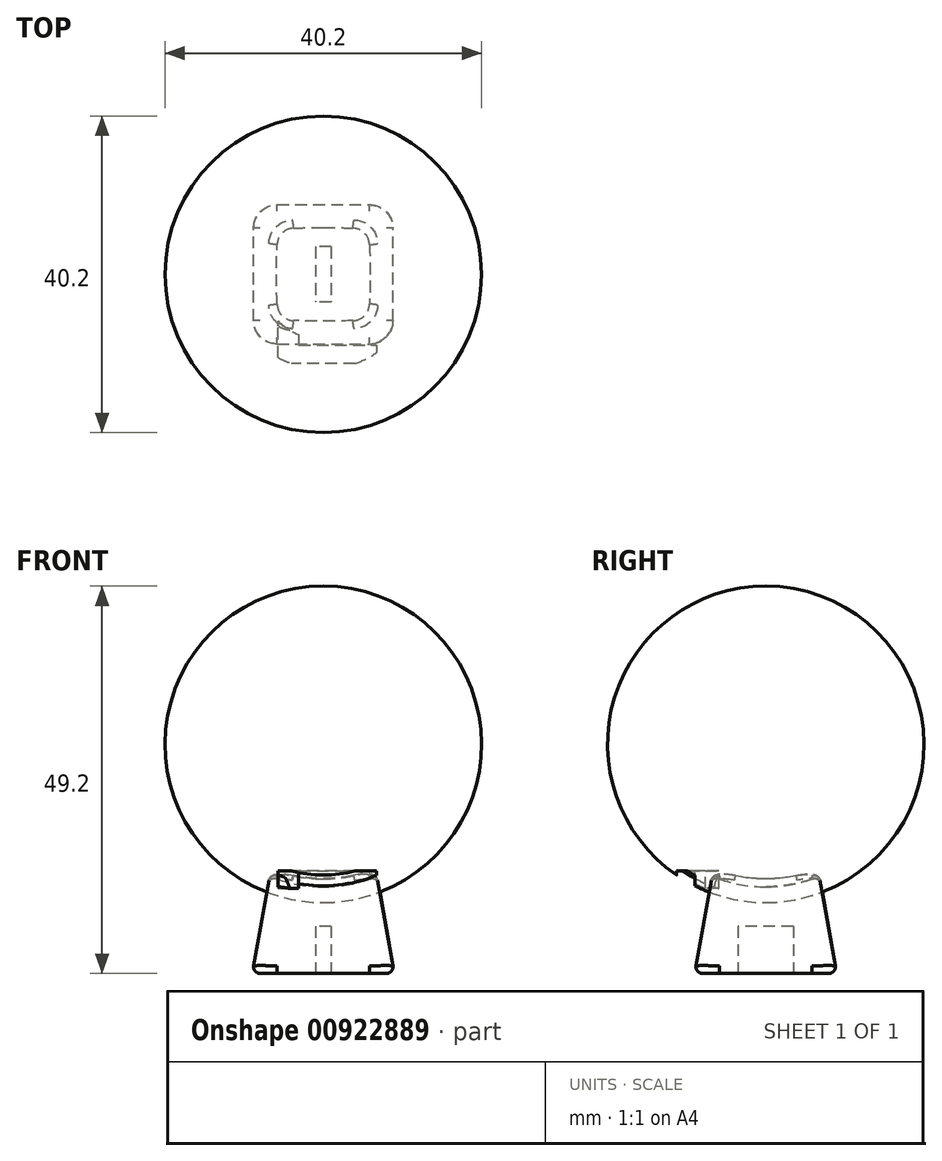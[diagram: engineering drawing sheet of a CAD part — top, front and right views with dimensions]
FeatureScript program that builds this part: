
annotation { "Feature Type Name" : "Feature", "Feature Type Description" : "" }
export const myFeature = defineFeature(function(context is Context, id is Id, definition is map)
    precondition{}
    {
        {
            var Q0;
            Q0=qCreatedBy(makeId("Top.planeOp"),FACE);
            var sketch = newSketch(context, id + "F0", { "sketchPlane" : qUnion([Q0])});
            skLineSegment(sketch, "E0.bottom", {"start": v(9, 9) * mm, "end": v(-9, 9) * mm});
            skLineSegment(sketch, "E0.top", {"start": v(9, -9) * mm, "end": v(-9, -9) * mm});
            skLineSegment(sketch, "E0.left", {"start": v(9, 9) * mm, "end": v(9, -9) * mm});
            skLineSegment(sketch, "E0.right", {"start": v(-9, 9) * mm, "end": v(-9, -9) * mm});
            skPoint(sketch, "E0.middle", {"position": v(0, 0) * mm});
            skLineSegment(sketch, "E1.bottom", {"start": v(1, 3.5) * mm, "end": v(-1, 3.5) * mm});
            skLineSegment(sketch, "E1.top", {"start": v(1, -3.5) * mm, "end": v(-1, -3.5) * mm});
            skLineSegment(sketch, "E1.left", {"start": v(1, 3.5) * mm, "end": v(1, -3.5) * mm});
            skLineSegment(sketch, "E1.right", {"start": v(-1, 3.5) * mm, "end": v(-1, -3.5) * mm});
            skLineSegment(sketch, "E2.bottom", {"start": v(1, 6.5) * mm, "end": v(-1, 6.5) * mm});
            skLineSegment(sketch, "E2.top", {"start": v(1, -6.5) * mm, "end": v(-1, -6.5) * mm});
            skLineSegment(sketch, "E2.left", {"start": v(1, 6.5) * mm, "end": v(1, -6.5) * mm});
            skLineSegment(sketch, "E2.right", {"start": v(-1, 6.5) * mm, "end": v(-1, -6.5) * mm});
            skSolve(sketch);
        }
        {
            var Q0;
            Q0=makeQuery(id+"F0.imprint","IMPRINT",FACE,{"disambiguationData":[TD([[makeQuery(id+"F0.imprint","IMPRINT",EDGE,{"derivedFrom":sQuery(id+"F0.wireOp",EDGE,"E0.bottom")}),1.0]])]});
            var Q1;
            {var subQ0=sQuery(id+"F0.wireOp",EDGE,"E1.bottom");Q1=makeQuery(id+"F0.imprint","IMPRINT",FACE,{"disambiguationData":[TD([[makeQuery(id+"F0.imprint","IMPRINT",EDGE,{"derivedFrom":subQ0}),-1.0]])]});}
            var Q2;
            Q2=makeQuery(id+"F0.imprint","IMPRINT",FACE,{"disambiguationData":[TD([[makeQuery(id+"F0.imprint","IMPRINT",EDGE,{"derivedFrom":sQuery(id+"F0.wireOp",EDGE,"E1.bottom")}),1.0]])]});
            var Q3;
            {var subQ0=sQuery(id+"F0.wireOp",EDGE,"E1.top");Q3=makeQuery(id+"F0.imprint","IMPRINT",FACE,{"disambiguationData":[TD([[makeQuery(id+"F0.imprint","IMPRINT",EDGE,{"derivedFrom":subQ0}),1.0]])]});}
            extrude(context, id + "F1", {"entities" : qUnion([Q0, Q1, Q2, Q3]), "depth" : 13 * mm, "offsetDistance" : 25 * mm, "hasDraft" : true, "draftAngle" : 10 * degree, "draftPullDirection" : true});
        }
        {
            var Q0;
            Q0=makeQuery(id+"F1.opExtrude","SWEPT_EDGE",EDGE,{"disambiguationData":[OSD([sQuery(id+"F0.wireOp",EDGE,"E0.top"),sQuery(id+"F0.wireOp",EDGE,"E0.right")])]});
            var Q1;
            Q1=makeQuery(id+"F1.opExtrude","SWEPT_EDGE",EDGE,{"disambiguationData":[OSD([sQuery(id+"F0.wireOp",EDGE,"E0.bottom"),sQuery(id+"F0.wireOp",EDGE,"E0.right")])]});
            var Q2;
            Q2=makeQuery(id+"F1.opExtrude","SWEPT_EDGE",EDGE,{"disambiguationData":[OSD([sQuery(id+"F0.wireOp",EDGE,"E0.top"),sQuery(id+"F0.wireOp",EDGE,"E0.left")])]});
            var Q3;
            Q3=makeQuery(id+"F1.opExtrude","SWEPT_EDGE",EDGE,{"disambiguationData":[OSD([sQuery(id+"F0.wireOp",EDGE,"E0.bottom"),sQuery(id+"F0.wireOp",EDGE,"E0.left")])]});
            fillet(context, id + "F2", {"entities" : qUnion([Q0, Q1, Q2, Q3]), "radius" : 3 * mm, "tangentPropagation" : true, "allowEdgeOverflow" : false});
        }
        {
            var Q0;
            Q0=makeQuery(id+"F1.opExtrude","CAP_FACE",FACE,{"disambiguationData":[OSD([sQuery(id+"F0.wireOp",EDGE,"E0.bottom"),sQuery(id+"F0.wireOp",EDGE,"E0.top"),sQuery(id+"F0.wireOp",EDGE,"E0.left"),sQuery(id+"F0.wireOp",EDGE,"E0.right")])],"isStart":false});
            var sketch = newSketch(context, id + "F3", { "sketchPlane" : qUnion([Q0])});
            skCircle(sketch, "E3", {"center": v(0, 0) * mm, "radius": 8.27 * mm});
            skText(sketch, "E4", { "text": "E", "fontName": "OpenSans-Regular.ttf"});
            const initialGuessF3  = {"E4": [-0.00882, -0.01133, 1, 0, 0.02265]};
            skSetInitialGuess(sketch, initialGuessF3);
            skSolve(sketch);
        }
        {
            var Q0;
            Q0=qCreatedBy(makeId("Right.planeOp"),FACE);
            var sketch = newSketch(context, id + "F4", { "sketchPlane" : qUnion([Q0])});
            skCircle(sketch, "E5", {"center": v(0, 29.1) * mm, "radius": 18.1 * mm});
            skLineSegment(sketch, "E6", {"start": v(0, 47.2) * mm, "end": v(0, 11) * mm});
            skCircle(sketch, "E7", {"center": v(0, 13) * mm, "radius": 8.27 * mm, "construction": true});
            skPoint(sketch, "E8.0", {"position": v(5.85, 13) * mm});
            skPoint(sketch, "E9", {"position": v(8.27, 13) * mm});
            skCircle(sketch, "E10", {"center": v(0, 29.1) * mm, "radius": 20.1 * mm});
            skLineSegment(sketch, "E11", {"start": v(0, 11) * mm, "end": v(0, 9) * mm});
            skLineSegment(sketch, "E12", {"start": v(0, 47.2) * mm, "end": v(0, 49.2) * mm});
            skSolve(sketch);
        }
        {
            var Q0;
            {var subQ0=sQuery(id+"F4.wireOp",EDGE,"E6");Q0=makeQuery(id+"F4.imprint","IMPRINT",FACE,{"disambiguationData":[TD([[makeQuery(id+"F4.imprint","IMPRINT",EDGE,{"derivedFrom":subQ0}),-1.0]])]});}
            var Q1;
            Q1=sQuery(id+"F4.wireOp",EDGE,"E6");
            revolve(context, id + "F5", {"operationType" : NewBodyOperationType.REMOVE, "surfaceOperationType" : NewSurfaceOperationType.NEW, "entities" : qUnion([Q0]), "axis" : qUnion([Q1]), "revolveType" : RevolveType.FULL, "oppositeDirection" : true});
        }
        {
            var Q0;
            Q0=makeQuery(id+"F5.boolean.opBoolean","INTERSECT",EDGE,{"derivedFrom":[makeQuery(id+"F2.opFillet","BLEND_FACE",FACE,{"disambiguationData":[OSD([sQuery(id+"F0.wireOp",EDGE,"E0.bottom"),sQuery(id+"F0.wireOp",EDGE,"E0.right")])]}),makeQuery(id+"F5.opRevolve","SWEPT_FACE",FACE,{"disambiguationData":[OSD([sQuery(id+"F4.wireOp",EDGE,"E5")])]})]});
            fillet(context, id + "F6", {"entities" : qUnion([Q0]), "radius" : 0.8 * mm, "tangentPropagation" : true, "allowEdgeOverflow" : false});
        }
        {
            var Q0;
            {var subQ3=sQuery(id+"F4.wireOp",EDGE,"E11");Q0=makeQuery(id+"F4.imprint","IMPRINT",FACE,{"disambiguationData":[TD([[makeQuery(id+"F4.imprint","IMPRINT",EDGE,{"derivedFrom":subQ3}),1.0]])]});}
            var Q1;
            {var subQ0=sQuery(id+"F4.wireOp",EDGE,"E6");Q1=makeQuery(id+"F4.imprint","IMPRINT",FACE,{"disambiguationData":[TD([[makeQuery(id+"F4.imprint","IMPRINT",EDGE,{"derivedFrom":subQ0}),1.0]])]});}
            var Q2;
            Q2=sQuery(id+"F4.wireOp",EDGE,"E6");
            revolve(context, id + "F7", {"surfaceOperationType" : NewSurfaceOperationType.NEW, "entities" : qUnion([Q0, Q1]), "axis" : qUnion([Q2]), "revolveType" : RevolveType.FULL});
        }
        {
            var Q0;
            Q0=makeQuery(id+"F3.imprint","IMPRINT",FACE,{"disambiguationData":[TD([[makeQuery(id+"F3.imprint","IMPRINT",EDGE,{"derivedFrom":sQuery(id+"F3.wireOp",EDGE,"E4.sketch_text.stroke-0")}),-1.0]])]});
            var Q1;
            Q1=makeQuery(id+"F7.opRevolve","SWEPT_BODY",BODY,{"disambiguationData":[OSD([sQuery(id+"F4.wireOp",EDGE,"E6"),sQuery(id+"F4.wireOp",EDGE,"E10"),sQuery(id+"F4.wireOp",EDGE,"E11"),sQuery(id+"F4.wireOp",EDGE,"E12")])]});
            extrude(context, id + "F8", {"entities" : qUnion([Q0]), "operationType" : NewBodyOperationType.REMOVE, "endBound" : BoundingType.UP_TO_BODY, "oppositeDirection" : true, "depth" : 2 * mm, "endBoundEntityBody" : qUnion([Q1]), "offsetDistance" : 25 * mm});
        }
        {
            var Q0;
            Q0=makeQuery(id+"F0.imprint","IMPRINT",FACE,{"disambiguationData":[TD([[makeQuery(id+"F0.imprint","IMPRINT",EDGE,{"derivedFrom":sQuery(id+"F0.wireOp",EDGE,"E1.bottom")}),1.0]])]});
            extrude(context, id + "F9", {"entities" : qUnion([Q0]), "operationType" : NewBodyOperationType.REMOVE, "depth" : 6 * mm, "offsetDistance" : 25 * mm});
        }
        {
            var Q0;
            Q0=makeQuery(id+"F1.opExtrude","CAP_EDGE",EDGE,{"disambiguationData":[OSD([sQuery(id+"F0.wireOp",EDGE,"E0.left")])],"isStart":true});
            var Q1;
            Q1=makeQuery(id+"F9.boolean.opBoolean","COPY",EDGE,{"derivedFrom":makeQuery(id+"F9.opExtrude","CAP_EDGE",EDGE,{"disambiguationData":[OSD([sQuery(id+"F0.wireOp",EDGE,"E1.bottom")])],"isStart":true})});
            fillet(context, id + "F10", {"entities" : qUnion([Q0, Q1]), "radius" : .8 * mm, "tangentPropagation" : true, "allowEdgeOverflow" : false});
        }
    });
